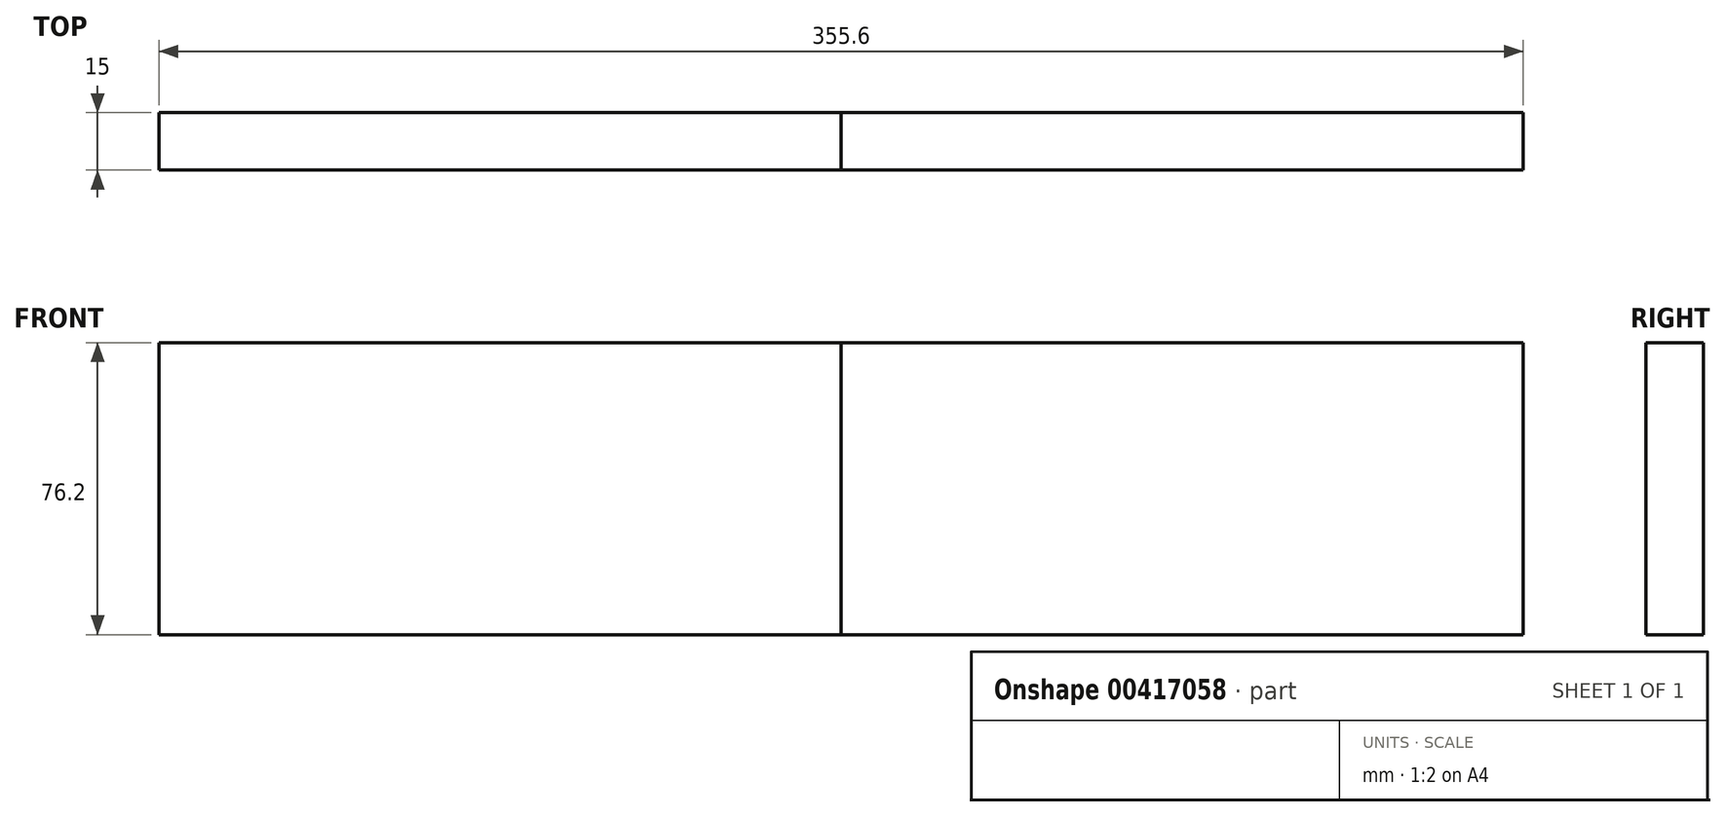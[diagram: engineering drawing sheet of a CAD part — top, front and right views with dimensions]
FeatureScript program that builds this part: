
annotation { "Feature Type Name" : "Feature", "Feature Type Description" : "" }
export const myFeature = defineFeature(function(context is Context, id is Id, definition is map)
    precondition{}
    {
        {
            var Q0;
            Q0=qCreatedBy(makeId("Front.planeOp"),FACE);
            var sketch = newSketch(context, id + "F0", { "sketchPlane" : qUnion([Q0])});
            skLineSegment(sketch, "E0.bottom", {"start": v(-94.53, 55.78) * mm, "end": v(83.27, 55.78) * mm});
            skLineSegment(sketch, "E0.top", {"start": v(-94.53, -20.42) * mm, "end": v(83.27, -20.42) * mm});
            skLineSegment(sketch, "E0.left", {"start": v(-94.53, 55.78) * mm, "end": v(-94.53, -20.42) * mm});
            skLineSegment(sketch, "E0.right", {"start": v(83.27, 55.78) * mm, "end": v(83.27, -20.42) * mm});
            skSolve(sketch);
        }
        {
            var Q0;
            Q0=makeQuery(id+"F0.imprint","IMPRINT",FACE,{"disambiguationData":[TD([[makeQuery(id+"F0.imprint","IMPRINT",EDGE,{"derivedFrom":sQuery(id+"F0.wireOp",EDGE,"E0.bottom")}),-1.0]])]});
            extrude(context, id + "F1", {"entities" : qUnion([Q0]), "depth" : 15 * mm});
        }
        {
            var Q0;
            Q0=makeQuery(id+"F1.opExtrude","SWEPT_BODY",BODY,{"disambiguationData":[OSD([sQuery(id+"F0.wireOp",EDGE,"E0.bottom"),sQuery(id+"F0.wireOp",EDGE,"E0.top"),sQuery(id+"F0.wireOp",EDGE,"E0.left"),sQuery(id+"F0.wireOp",EDGE,"E0.right")])]});
            var Q1;
            Q1=makeQuery(id+"F1.opExtrude","CAP_EDGE",EDGE,{"disambiguationData":[OSD([sQuery(id+"F0.wireOp",EDGE,"E0.bottom")])],"isStart":false});
            transform(context, id + "F2", {"entities" : qUnion([Q0]), "transformType" : TransformType.TRANSLATION_ENTITY, "oppositeDirectionEntity" : true, "transformLine" : qUnion([Q1]), "makeCopy" : true});
        }
    });
